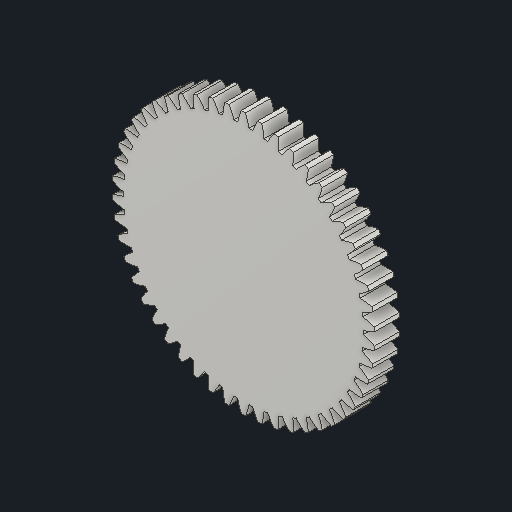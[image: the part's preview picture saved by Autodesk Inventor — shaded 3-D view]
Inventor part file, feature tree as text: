
AUTODESK INVENTOR PART (.ipt)
format: ipt  version: 2024.1 (Build 281209000, 209)  size: 328,192 bytes
history: native  units: mm (DEFAULTED — no unit token found)
features: plane x3, other x3, extrude x1, sketch x1
ambient origin geometry x8: Origin, YZ Plane, XZ Plane, XY Plane, X Axis, Y Axis, Z Axis, Center Point
bodies: Solid1 (feature_tree)
feature tree (8):
  extrude  "Extrusion1"  Depth=3.81mm TaperAngle=0.0deg
  plane  "Work Plane1"
  plane  "Work Plane2"
  plane  "Work Plane3"
  other  "Spur Gear"
  sketch  "Sketch1"  dims[d0=39.624mm d1=3.81mm d2=0.0mm d3=38.1mm d4=76.2mm d5=0.0mm d6=0.0mm d7=0.628319mm d9=0.0mm d14=0.0mm d15=23.622mm d16=0.0mm d17=0.0mm d18=0.0mm d19=23.622mm]
  other  "Srf1"
  other  "Pitch Diameter"
